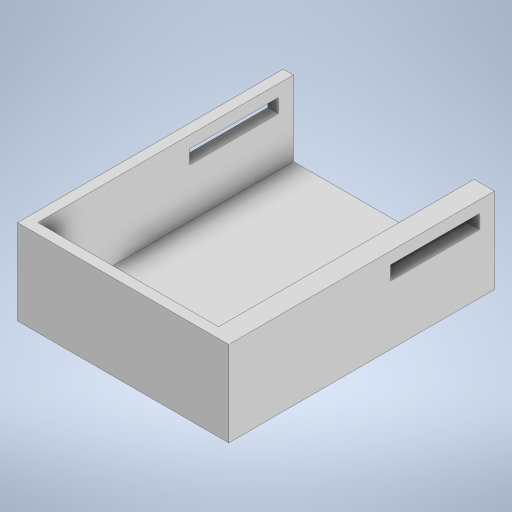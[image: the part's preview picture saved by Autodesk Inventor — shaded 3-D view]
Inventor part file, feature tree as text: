
AUTODESK INVENTOR PART (.ipt)
format: ipt  version: 2023 (Build 270158000, 158)  size: 245,760 bytes
history: native  units: in
note: dims shown in document units (in); Inventor stores cm internally (conversion verified against a paired STEP export)
features: sketch x5, extrude x4, shell x1
ambient origin geometry x8: Origin, YZ Plane, XZ Plane, XY Plane, X Axis, Y Axis, Z Axis, Center Point
bodies: Solid1 (feature_tree)
feature tree (10):
  extrude  "Extrusion1"  Depth=3.0709in
  shell  "Shell1"  Thickness=0.9843in
  sketch  "Sketch4"  dims[d4=0.1181in d17=0.3937in d18=0.0in]
  extrude  "Extrusion3"  Depth=0.1181in TaperAngle=0.0deg
  sketch  "Sketch6"  dims[d21=0.1772in d22=0.689in]
  extrude  "Extrusion5"  Depth=0.1575in
  extrude  "Extrusion6"  Depth=0.689in
  sketch  "Sketch2"  dims[d0=2.3228in d1=3.0709in d2=0.9843in d3=0.0in]
  sketch  "Sketch5"  dims[d19=1.0236in d20=0.1575in]
  sketch  "Sketch7"  dims[d25=0.1181in d26=0.0in d27=0.0in d28=0.0in d13=0.0197in d14=0.0344in d15=0.0197in d16=0.0344in]
